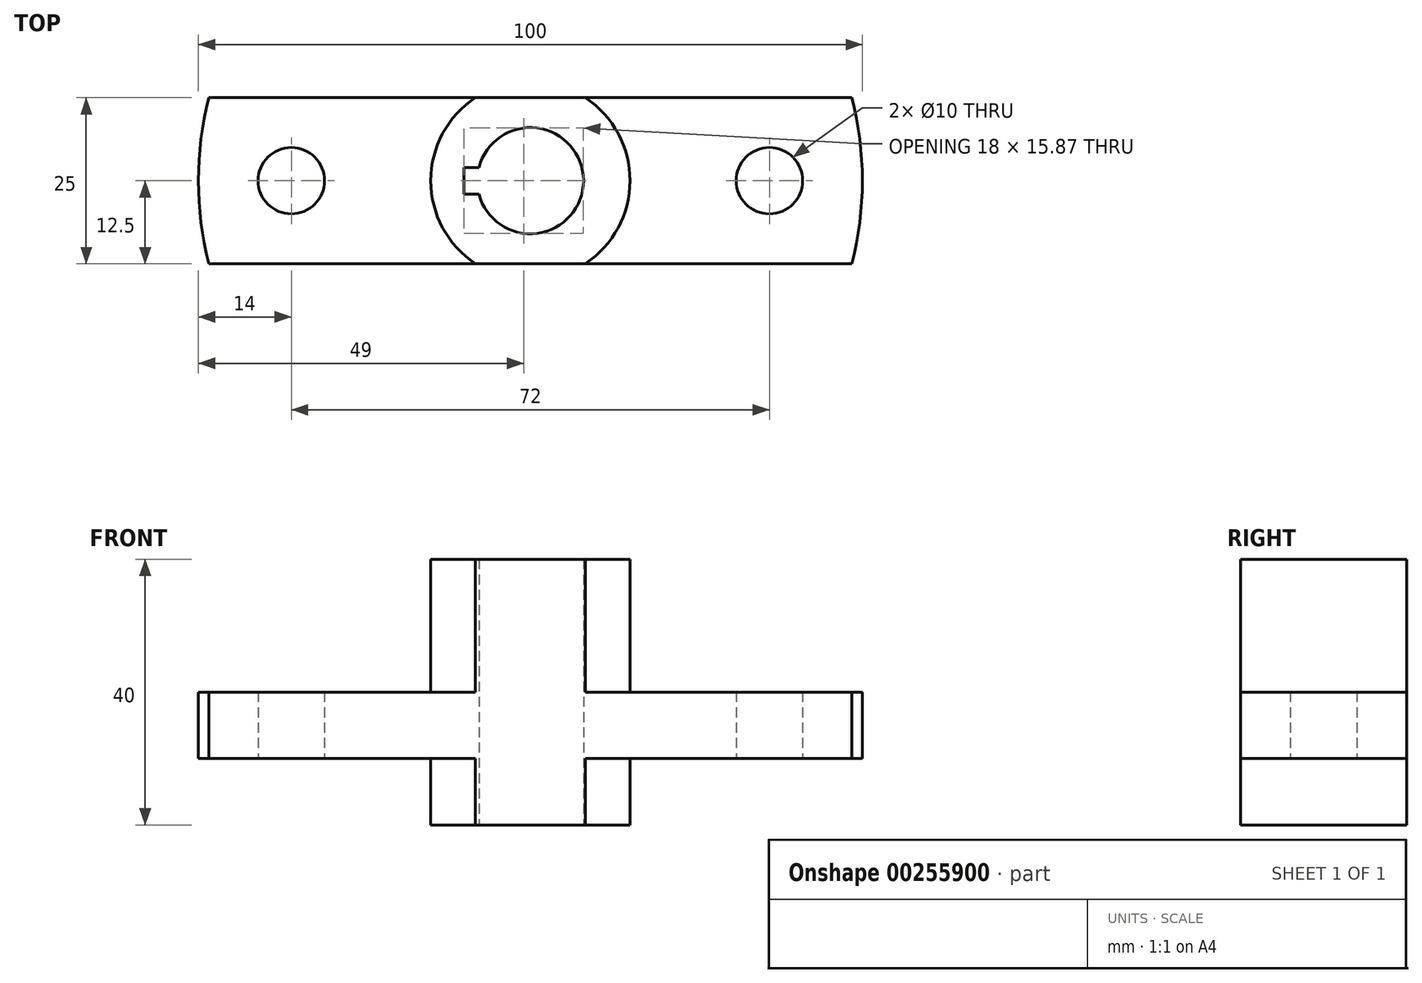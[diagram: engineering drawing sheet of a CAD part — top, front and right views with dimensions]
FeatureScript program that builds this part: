
annotation { "Feature Type Name" : "Feature", "Feature Type Description" : "" }
export const myFeature = defineFeature(function(context is Context, id is Id, definition is map)
    precondition{}
    {
        {
            var Q0;
            Q0=qCreatedBy(makeId("Top.planeOp"),FACE);
            var sketch = newSketch(context, id + "F0", { "sketchPlane" : qUnion([Q0])});
            skArc(sketch, "E0", {"start": v(0, -8) * mm, "mid": v(8, 0) * mm, "end": v(0, 8) * mm});
            skArc(sketch, "E1", {"start": v(48.41, -12.5) * mm, "mid": v(50, 0) * mm, "end": v(48.41, 12.5) * mm});
            skLineSegment(sketch, "E2", {"start": v(0, 12.5) * mm, "end": v(48.41, 12.5) * mm});
            skLineSegment(sketch, "E3", {"start": v(0, -12.5) * mm, "end": v(48.41, -12.5) * mm});
            skArc(sketch, "E4.trimOffspring", {"start": v(8.3, -12.5) * mm, "mid": v(15, 0) * mm, "end": v(8.3, 12.5) * mm});
            skLineSegment(sketch, "E5", {"start": v(0, 12.5) * mm, "end": v(0, -12.5) * mm});
            skCircle(sketch, "E6", {"center": v(36, 0) * mm, "radius": 5 * mm});
            skPoint(sketch, "E6.centerSnap0", {"position": v(15, 0) * mm});
            skSolve(sketch);
        }
        {
            var Q0;
            {var subQ6=sQuery(id+"F0.wireOp",EDGE,"E0");Q0=makeQuery(id+"F0.imprint","IMPRINT",FACE,{"disambiguationData":[TD([[makeQuery(id+"F0.imprint","IMPRINT",EDGE,{"derivedFrom":subQ6}),-1.0]])]});}
            extrude(context, id + "F1", {"entities" : qUnion([Q0]), "depth" : 30 * mm, "hasSecondDirection" : true, "secondDirectionOppositeDirection" : true, "secondDirectionDepth" : 10 * mm});
        }
        {
            var Q0;
            {var subQ2=sQuery(id+"F0.wireOp",EDGE,"E1");Q0=makeQuery(id+"F0.imprint","IMPRINT",FACE,{"disambiguationData":[TD([[makeQuery(id+"F0.imprint","IMPRINT",EDGE,{"derivedFrom":subQ2}),1.0]])]});}
            extrude(context, id + "F2", {"entities" : qUnion([Q0]), "operationType" : NewBodyOperationType.ADD, "depth" : 10 * mm});
        }
        {
            var Q0;
            Q0=makeQuery(id+"F1.opExtrude","SWEPT_BODY",BODY,{"disambiguationData":[OSD([sQuery(id+"F0.wireOp",EDGE,"E0"),sQuery(id+"F0.wireOp",EDGE,"E2"),sQuery(id+"F0.wireOp",EDGE,"E3"),sQuery(id+"F0.wireOp",EDGE,"E4.trimOffspring"),sQuery(id+"F0.wireOp",EDGE,"E5")])]});
            var Q1;
            Q1=qCreatedBy(makeId("Right.planeOp"),FACE);
            mirror(context, id + "F3", {"operationType" : NewBodyOperationType.ADD, "entities" : qUnion([Q0]), "mirrorPlane" : qUnion([Q1])});
        }
        {
            var Q0;
            Q0=qCreatedBy(makeId("Top.planeOp"),FACE);
            var sketch = newSketch(context, id + "F4", { "sketchPlane" : qUnion([Q0])});
            skLineSegment(sketch, "E7.bottom", {"start": v(-10, 2) * mm, "end": v(-2.82, 2) * mm});
            skLineSegment(sketch, "E7.top", {"start": v(-10, -2) * mm, "end": v(-2.82, -2) * mm});
            skLineSegment(sketch, "E7.left", {"start": v(-10, 2) * mm, "end": v(-10, -2) * mm});
            skLineSegment(sketch, "E7.right", {"start": v(-2.82, 2) * mm, "end": v(-2.82, -2) * mm});
            skPoint(sketch, "E7.middle", {"position": v(-6.4, 0) * mm});
            skLineSegment(sketch, "E8", {"start": v(-10, -2) * mm, "end": v(-10, 2) * mm});
            skSolve(sketch);
        }
        {
            var Q0;
            Q0=makeQuery(id+"F4.imprint","IMPRINT",FACE,{"disambiguationData":[TD([[makeQuery(id+"F4.imprint","IMPRINT",EDGE,{"derivedFrom":sQuery(id+"F4.wireOp",EDGE,"E7.right")}),-1.0]])]});
            extrude(context, id + "F5", {"entities" : qUnion([Q0]), "operationType" : NewBodyOperationType.REMOVE, "endBound" : BoundingType.THROUGH_ALL, "oppositeDirection" : true, "depth" : 25 * mm, "hasSecondDirection" : true, "secondDirectionBound" : SecondDirectionBoundingType.THROUGH_ALL, "secondDirectionOppositeDirection" : false, "secondDirectionDepth" : 25 * mm});
        }
    });
